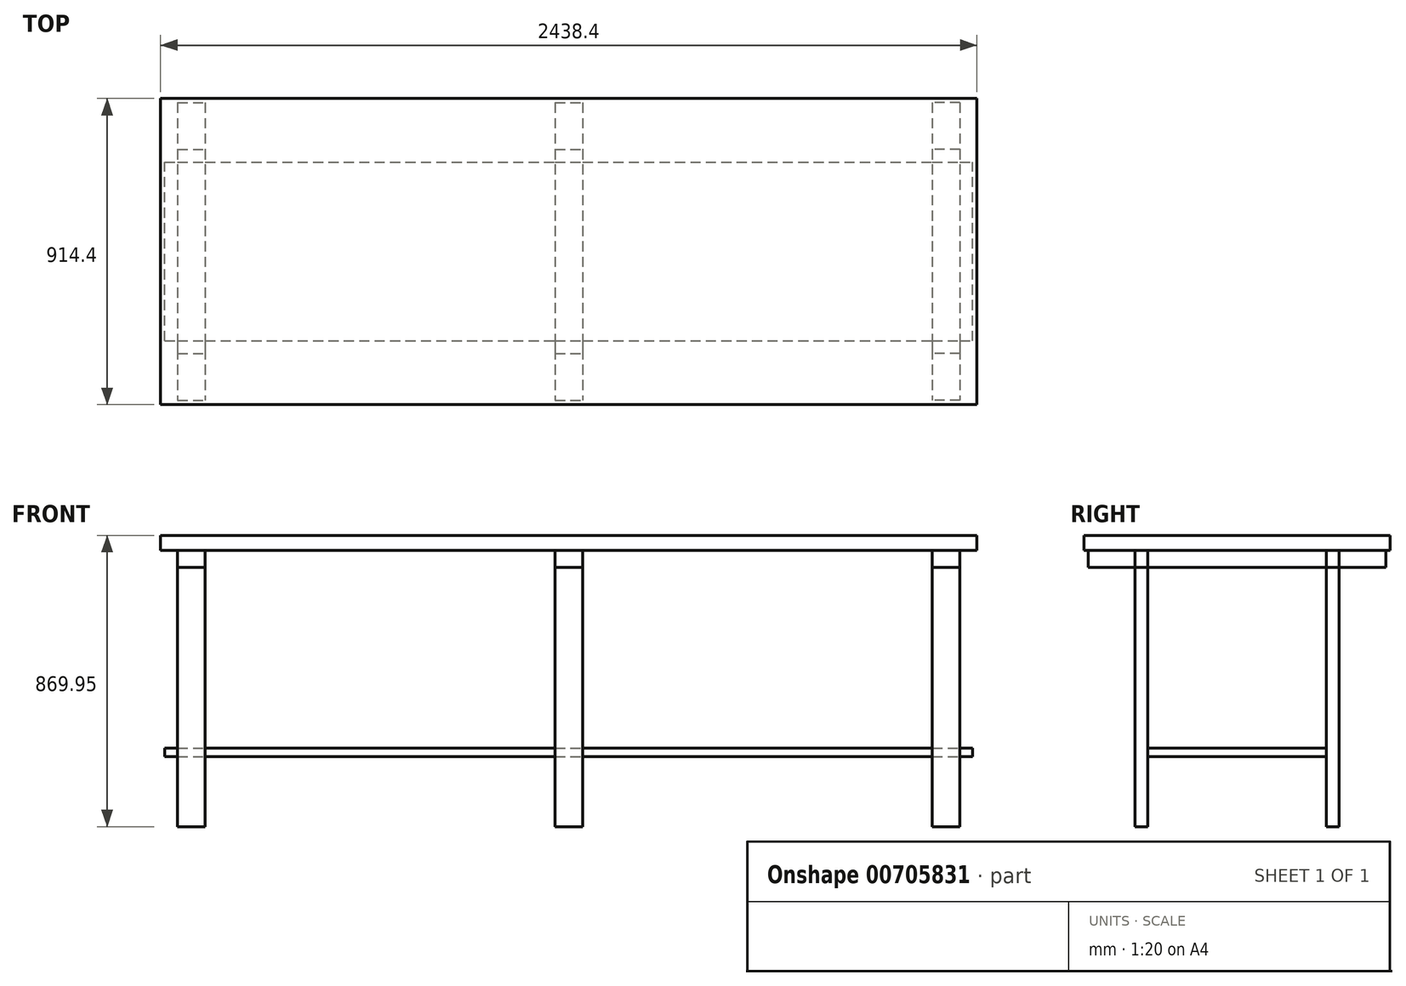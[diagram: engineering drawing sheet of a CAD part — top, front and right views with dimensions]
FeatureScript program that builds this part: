
annotation { "Feature Type Name" : "Feature", "Feature Type Description" : "" }
export const myFeature = defineFeature(function(context is Context, id is Id, definition is map)
    precondition{}
    {
        {
            var Q0;
            Q0=qCreatedBy(makeId("Top.planeOp"),FACE);
            var sketch = newSketch(context, id + "F0", { "sketchPlane" : qUnion([Q0])});
            skLineSegment(sketch, "E0.bottom", {"start": v(0, 0) * mm, "end": v(2438.4, 0) * mm});
            skLineSegment(sketch, "E0.top", {"start": v(0, 914.4) * mm, "end": v(2438.4, 914.4) * mm});
            skLineSegment(sketch, "E0.left", {"start": v(0, 0) * mm, "end": v(0, 914.4) * mm});
            skLineSegment(sketch, "E0.right", {"start": v(2438.4, 0) * mm, "end": v(2438.4, 914.4) * mm});
            skLineSegment(sketch, "E1.bottom", {"start": v(50.8, 901.7) * mm, "end": v(133.35, 901.7) * mm});
            skLineSegment(sketch, "E1.top", {"start": v(50.8, 12.7) * mm, "end": v(133.35, 12.7) * mm});
            skLineSegment(sketch, "E1.left", {"start": v(50.8, 901.7) * mm, "end": v(50.8, 12.7) * mm});
            skLineSegment(sketch, "E1.right", {"start": v(133.35, 901.7) * mm, "end": v(133.35, 12.7) * mm});
            skLineSegment(sketch, "E2", {"start": v(1219.2, 914.4) * mm, "end": v(1219.2, 0) * mm, "construction": true});
            skLineSegment(sketch, "E3", {"start": v(50.8, 762) * mm, "end": v(133.35, 762) * mm});
            skLineSegment(sketch, "E4", {"start": v(50.8, 723.9) * mm, "end": v(133.35, 723.9) * mm});
            skLineSegment(sketch, "E5", {"start": v(0, 457.2) * mm, "end": v(2438.4, 457.2) * mm, "construction": true});
            skLineSegment(sketch, "E6.MirrorCS", {"start": v(50.8, 152.4) * mm, "end": v(133.35, 152.4) * mm});
            skLineSegment(sketch, "E7.MirrorCS", {"start": v(50.8, 190.5) * mm, "end": v(133.35, 190.5) * mm});
            skLineSegment(sketch, "E8.MirrorCS", {"start": v(2387.6, 901.7) * mm, "end": v(2305.05, 901.7) * mm});
            skLineSegment(sketch, "E9.MirrorCS", {"start": v(2387.6, 12.7) * mm, "end": v(2305.05, 12.7) * mm});
            skLineSegment(sketch, "E10.MirrorCS", {"start": v(2387.6, 152.4) * mm, "end": v(2305.05, 152.4) * mm});
            skLineSegment(sketch, "E11.MirrorCS", {"start": v(2387.6, 190.5) * mm, "end": v(2305.05, 190.5) * mm});
            skLineSegment(sketch, "E12.MirrorCS", {"start": v(2387.6, 723.9) * mm, "end": v(2305.05, 723.9) * mm});
            skLineSegment(sketch, "E13.MirrorCS", {"start": v(2387.6, 762) * mm, "end": v(2305.05, 762) * mm});
            skLineSegment(sketch, "E14.MirrorCS", {"start": v(2387.6, 901.7) * mm, "end": v(2387.6, 12.7) * mm});
            skLineSegment(sketch, "E15.MirrorCS", {"start": v(2305.05, 901.7) * mm, "end": v(2305.05, 12.7) * mm});
            skLineSegment(sketch, "E16.bottom", {"start": v(1177.92, 901.7) * mm, "end": v(1260.48, 901.7) * mm});
            skLineSegment(sketch, "E16.top", {"start": v(1177.92, 12.7) * mm, "end": v(1260.48, 12.7) * mm});
            skLineSegment(sketch, "E16.left", {"start": v(1177.92, 901.7) * mm, "end": v(1177.92, 12.7) * mm});
            skLineSegment(sketch, "E16.right", {"start": v(1260.47, 901.7) * mm, "end": v(1260.47, 12.7) * mm});
            skLineSegment(sketch, "E17", {"start": v(1177.92, 762) * mm, "end": v(1260.48, 762) * mm});
            skLineSegment(sketch, "E18", {"start": v(1177.92, 723.9) * mm, "end": v(1260.48, 723.9) * mm});
            skLineSegment(sketch, "E19.MirrorCS", {"start": v(1177.92, 152.4) * mm, "end": v(1260.48, 152.4) * mm});
            skLineSegment(sketch, "E20.MirrorCS", {"start": v(1177.92, 190.5) * mm, "end": v(1260.48, 190.5) * mm});
            skPoint(sketch, "E21", {"position": v(1219.2, 901.7) * mm});
            skSolve(sketch);
        }
        {
            var Q0;
            Q0 = qSketchRegion(id + "F0", true);
            var Q1;
            {var subQ0=sQuery(id+"F0.wireOp",EDGE,"E1.bottom");Q1=makeQuery(id+"F0.imprint","IMPRINT",FACE,{"disambiguationData":[TD([[makeQuery(id+"F0.imprint","IMPRINT",EDGE,{"derivedFrom":subQ0}),-1.0]])]});}
            var Q2;
            {var subQ0=sQuery(id+"F0.wireOp",EDGE,"E3");Q2=makeQuery(id+"F0.imprint","IMPRINT",FACE,{"disambiguationData":[TD([[makeQuery(id+"F0.imprint","IMPRINT",EDGE,{"derivedFrom":subQ0}),-1.0]])]});}
            var Q3;
            {var subQ0=sQuery(id+"F0.wireOp",EDGE,"E4");Q3=makeQuery(id+"F0.imprint","IMPRINT",FACE,{"disambiguationData":[TD([[makeQuery(id+"F0.imprint","IMPRINT",EDGE,{"derivedFrom":subQ0}),-1.0]])]});}
            var Q4;
            {var subQ0=sQuery(id+"F0.wireOp",EDGE,"E6.MirrorCS");Q4=makeQuery(id+"F0.imprint","IMPRINT",FACE,{"disambiguationData":[TD([[makeQuery(id+"F0.imprint","IMPRINT",EDGE,{"derivedFrom":subQ0}),1.0]])]});}
            var Q5;
            {var subQ0=sQuery(id+"F0.wireOp",EDGE,"E1.top");Q5=makeQuery(id+"F0.imprint","IMPRINT",FACE,{"disambiguationData":[TD([[makeQuery(id+"F0.imprint","IMPRINT",EDGE,{"derivedFrom":subQ0}),1.0]])]});}
            var Q6;
            {var subQ0=sQuery(id+"F0.wireOp",EDGE,"E16.top");Q6=makeQuery(id+"F0.imprint","IMPRINT",FACE,{"disambiguationData":[TD([[makeQuery(id+"F0.imprint","IMPRINT",EDGE,{"derivedFrom":subQ0}),1.0]])]});}
            var Q7;
            {var subQ0=sQuery(id+"F0.wireOp",EDGE,"E19.MirrorCS");Q7=makeQuery(id+"F0.imprint","IMPRINT",FACE,{"disambiguationData":[TD([[makeQuery(id+"F0.imprint","IMPRINT",EDGE,{"derivedFrom":subQ0}),1.0]])]});}
            var Q8;
            {var subQ0=sQuery(id+"F0.wireOp",EDGE,"E18");Q8=makeQuery(id+"F0.imprint","IMPRINT",FACE,{"disambiguationData":[TD([[makeQuery(id+"F0.imprint","IMPRINT",EDGE,{"derivedFrom":subQ0}),-1.0]])]});}
            var Q9;
            {var subQ0=sQuery(id+"F0.wireOp",EDGE,"E17");Q9=makeQuery(id+"F0.imprint","IMPRINT",FACE,{"disambiguationData":[TD([[makeQuery(id+"F0.imprint","IMPRINT",EDGE,{"derivedFrom":subQ0}),-1.0]])]});}
            var Q10;
            {var subQ0=sQuery(id+"F0.wireOp",EDGE,"E16.bottom");Q10=makeQuery(id+"F0.imprint","IMPRINT",FACE,{"disambiguationData":[TD([[makeQuery(id+"F0.imprint","IMPRINT",EDGE,{"derivedFrom":subQ0}),-1.0]])]});}
            var Q11;
            {var subQ0=sQuery(id+"F0.wireOp",EDGE,"E8.MirrorCS");Q11=makeQuery(id+"F0.imprint","IMPRINT",FACE,{"disambiguationData":[TD([[makeQuery(id+"F0.imprint","IMPRINT",EDGE,{"derivedFrom":subQ0}),1.0]])]});}
            var Q12;
            {var subQ0=sQuery(id+"F0.wireOp",EDGE,"E12.MirrorCS");Q12=makeQuery(id+"F0.imprint","IMPRINT",FACE,{"disambiguationData":[TD([[makeQuery(id+"F0.imprint","IMPRINT",EDGE,{"derivedFrom":subQ0}),-1.0]])]});}
            var Q13;
            {var subQ0=sQuery(id+"F0.wireOp",EDGE,"E11.MirrorCS");Q13=makeQuery(id+"F0.imprint","IMPRINT",FACE,{"disambiguationData":[TD([[makeQuery(id+"F0.imprint","IMPRINT",EDGE,{"derivedFrom":subQ0}),-1.0]])]});}
            var Q14;
            {var subQ0=sQuery(id+"F0.wireOp",EDGE,"E10.MirrorCS");Q14=makeQuery(id+"F0.imprint","IMPRINT",FACE,{"disambiguationData":[TD([[makeQuery(id+"F0.imprint","IMPRINT",EDGE,{"derivedFrom":subQ0}),-1.0]])]});}
            var Q15;
            {var subQ0=sQuery(id+"F0.wireOp",EDGE,"E9.MirrorCS");Q15=makeQuery(id+"F0.imprint","IMPRINT",FACE,{"disambiguationData":[TD([[makeQuery(id+"F0.imprint","IMPRINT",EDGE,{"derivedFrom":subQ0}),-1.0]])]});}
            extrude(context, id + "F1", {"entities" : qUnion([Q0, Q1, Q2, Q3, Q4, Q5, Q6, Q7, Q8, Q9, Q10, Q11, Q12, Q13, Q14, Q15]), "depth" : 44.45 * mm, "offsetDistance" : 25.4 * mm});
        }
        {
            var Q0;
            {var subQ0=sQuery(id+"F0.wireOp",EDGE,"E1.top");Q0=makeQuery(id+"F0.imprint","IMPRINT",FACE,{"disambiguationData":[TD([[makeQuery(id+"F0.imprint","IMPRINT",EDGE,{"derivedFrom":subQ0}),1.0]])]});}
            var Q1;
            {var subQ0=sQuery(id+"F0.wireOp",EDGE,"E6.MirrorCS");Q1=makeQuery(id+"F0.imprint","IMPRINT",FACE,{"disambiguationData":[TD([[makeQuery(id+"F0.imprint","IMPRINT",EDGE,{"derivedFrom":subQ0}),1.0]])]});}
            var Q2;
            {var subQ0=sQuery(id+"F0.wireOp",EDGE,"E4");Q2=makeQuery(id+"F0.imprint","IMPRINT",FACE,{"disambiguationData":[TD([[makeQuery(id+"F0.imprint","IMPRINT",EDGE,{"derivedFrom":subQ0}),-1.0]])]});}
            var Q3;
            {var subQ0=sQuery(id+"F0.wireOp",EDGE,"E3");Q3=makeQuery(id+"F0.imprint","IMPRINT",FACE,{"disambiguationData":[TD([[makeQuery(id+"F0.imprint","IMPRINT",EDGE,{"derivedFrom":subQ0}),-1.0]])]});}
            var Q4;
            {var subQ0=sQuery(id+"F0.wireOp",EDGE,"E1.bottom");Q4=makeQuery(id+"F0.imprint","IMPRINT",FACE,{"disambiguationData":[TD([[makeQuery(id+"F0.imprint","IMPRINT",EDGE,{"derivedFrom":subQ0}),-1.0]])]});}
            var Q5;
            {var subQ0=sQuery(id+"F0.wireOp",EDGE,"E16.top");Q5=makeQuery(id+"F0.imprint","IMPRINT",FACE,{"disambiguationData":[TD([[makeQuery(id+"F0.imprint","IMPRINT",EDGE,{"derivedFrom":subQ0}),1.0]])]});}
            var Q6;
            {var subQ0=sQuery(id+"F0.wireOp",EDGE,"E18");Q6=makeQuery(id+"F0.imprint","IMPRINT",FACE,{"disambiguationData":[TD([[makeQuery(id+"F0.imprint","IMPRINT",EDGE,{"derivedFrom":subQ0}),-1.0]])]});}
            var Q7;
            {var subQ0=sQuery(id+"F0.wireOp",EDGE,"E19.MirrorCS");Q7=makeQuery(id+"F0.imprint","IMPRINT",FACE,{"disambiguationData":[TD([[makeQuery(id+"F0.imprint","IMPRINT",EDGE,{"derivedFrom":subQ0}),1.0]])]});}
            var Q8;
            {var subQ0=sQuery(id+"F0.wireOp",EDGE,"E17");Q8=makeQuery(id+"F0.imprint","IMPRINT",FACE,{"disambiguationData":[TD([[makeQuery(id+"F0.imprint","IMPRINT",EDGE,{"derivedFrom":subQ0}),-1.0]])]});}
            var Q9;
            {var subQ0=sQuery(id+"F0.wireOp",EDGE,"E16.bottom");Q9=makeQuery(id+"F0.imprint","IMPRINT",FACE,{"disambiguationData":[TD([[makeQuery(id+"F0.imprint","IMPRINT",EDGE,{"derivedFrom":subQ0}),-1.0]])]});}
            var Q10;
            {var subQ0=sQuery(id+"F0.wireOp",EDGE,"E9.MirrorCS");Q10=makeQuery(id+"F0.imprint","IMPRINT",FACE,{"disambiguationData":[TD([[makeQuery(id+"F0.imprint","IMPRINT",EDGE,{"derivedFrom":subQ0}),-1.0]])]});}
            var Q11;
            {var subQ0=sQuery(id+"F0.wireOp",EDGE,"E10.MirrorCS");Q11=makeQuery(id+"F0.imprint","IMPRINT",FACE,{"disambiguationData":[TD([[makeQuery(id+"F0.imprint","IMPRINT",EDGE,{"derivedFrom":subQ0}),-1.0]])]});}
            var Q12;
            {var subQ0=sQuery(id+"F0.wireOp",EDGE,"E11.MirrorCS");Q12=makeQuery(id+"F0.imprint","IMPRINT",FACE,{"disambiguationData":[TD([[makeQuery(id+"F0.imprint","IMPRINT",EDGE,{"derivedFrom":subQ0}),-1.0]])]});}
            var Q13;
            {var subQ0=sQuery(id+"F0.wireOp",EDGE,"E12.MirrorCS");Q13=makeQuery(id+"F0.imprint","IMPRINT",FACE,{"disambiguationData":[TD([[makeQuery(id+"F0.imprint","IMPRINT",EDGE,{"derivedFrom":subQ0}),-1.0]])]});}
            var Q14;
            {var subQ0=sQuery(id+"F0.wireOp",EDGE,"E8.MirrorCS");Q14=makeQuery(id+"F0.imprint","IMPRINT",FACE,{"disambiguationData":[TD([[makeQuery(id+"F0.imprint","IMPRINT",EDGE,{"derivedFrom":subQ0}),1.0]])]});}
            extrude(context, id + "F2", {"entities" : qUnion([Q0, Q1, Q2, Q3, Q4, Q5, Q6, Q7, Q8, Q9, Q10, Q11, Q12, Q13, Q14]), "operationType" : NewBodyOperationType.ADD, "oppositeDirection" : true, "depth" : 50.8 * mm, "offsetDistance" : 25.4 * mm});
        }
        {
            var Q0;
            {var subQ0=sQuery(id+"F0.wireOp",EDGE,"E6.MirrorCS");Q0=makeQuery(id+"F0.imprint","IMPRINT",FACE,{"disambiguationData":[TD([[makeQuery(id+"F0.imprint","IMPRINT",EDGE,{"derivedFrom":subQ0}),1.0]])]});}
            var Q1;
            {var subQ0=sQuery(id+"F0.wireOp",EDGE,"E3");Q1=makeQuery(id+"F0.imprint","IMPRINT",FACE,{"disambiguationData":[TD([[makeQuery(id+"F0.imprint","IMPRINT",EDGE,{"derivedFrom":subQ0}),-1.0]])]});}
            var Q2;
            {var subQ0=sQuery(id+"F0.wireOp",EDGE,"E19.MirrorCS");Q2=makeQuery(id+"F0.imprint","IMPRINT",FACE,{"disambiguationData":[TD([[makeQuery(id+"F0.imprint","IMPRINT",EDGE,{"derivedFrom":subQ0}),1.0]])]});}
            var Q3;
            {var subQ0=sQuery(id+"F0.wireOp",EDGE,"E17");Q3=makeQuery(id+"F0.imprint","IMPRINT",FACE,{"disambiguationData":[TD([[makeQuery(id+"F0.imprint","IMPRINT",EDGE,{"derivedFrom":subQ0}),-1.0]])]});}
            var Q4;
            {var subQ0=sQuery(id+"F0.wireOp",EDGE,"E10.MirrorCS");Q4=makeQuery(id+"F0.imprint","IMPRINT",FACE,{"disambiguationData":[TD([[makeQuery(id+"F0.imprint","IMPRINT",EDGE,{"derivedFrom":subQ0}),-1.0]])]});}
            var Q5;
            {var subQ0=sQuery(id+"F0.wireOp",EDGE,"E12.MirrorCS");Q5=makeQuery(id+"F0.imprint","IMPRINT",FACE,{"disambiguationData":[TD([[makeQuery(id+"F0.imprint","IMPRINT",EDGE,{"derivedFrom":subQ0}),-1.0]])]});}
            extrude(context, id + "F3", {"entities" : qUnion([Q0, Q1, Q2, Q3, Q4, Q5]), "oppositeDirection" : true, "depth" : 825.5 * mm, "offsetDistance" : 25.4 * mm});
        }
        {
            var Q0;
            Q0=makeQuery(id+"F0.imprint","IMPRINT",FACE,{"disambiguationData":[TD([[makeQuery(id+"F0.imprint","IMPRINT",EDGE,{"derivedFrom":sQuery(id+"F0.wireOp",EDGE,"E0.bottom")}),1.0]])]});
            cPlane(context, id + "F4", {"entities" : qUnion([Q0]), "cplaneType" : CPlaneType.OFFSET, "offset" : 590.55 * mm, "oppositeDirection" : true, "width" : 152.4 * mm, "height" : 152.4 * mm});
        }
        {
            var Q0;
            Q0=qCreatedBy(id+"F4.planeOp",FACE);
            var sketch = newSketch(context, id + "F5", { "sketchPlane" : qUnion([Q0])});
            skLineSegment(sketch, "E22.0.0", {"start": v(50.8, 723.9) * mm, "end": v(50.8, 190.5) * mm});
            skLineSegment(sketch, "E22.0.1", {"start": v(50.8, 190.5) * mm, "end": v(133.35, 190.5) * mm});
            skLineSegment(sketch, "E22.0.2", {"start": v(133.35, 190.5) * mm, "end": v(133.35, 723.9) * mm});
            skLineSegment(sketch, "E22.0.3", {"start": v(133.35, 723.9) * mm, "end": v(50.8, 723.9) * mm});
            skLineSegment(sketch, "E23.0.0", {"start": v(2305.05, 190.5) * mm, "end": v(2387.6, 190.5) * mm});
            skLineSegment(sketch, "E23.0.1", {"start": v(2387.6, 190.5) * mm, "end": v(2387.6, 723.9) * mm});
            skLineSegment(sketch, "E23.0.2", {"start": v(2387.6, 723.9) * mm, "end": v(2305.05, 723.9) * mm});
            skLineSegment(sketch, "E23.0.3", {"start": v(2305.05, 723.9) * mm, "end": v(2305.05, 190.5) * mm});
            skLineSegment(sketch, "E24.bottom", {"start": v(12.7, 190.5) * mm, "end": v(2425.7, 190.5) * mm});
            skLineSegment(sketch, "E24.top", {"start": v(12.7, 723.9) * mm, "end": v(2425.7, 723.9) * mm});
            skLineSegment(sketch, "E24.left", {"start": v(12.7, 190.5) * mm, "end": v(12.7, 723.9) * mm});
            skLineSegment(sketch, "E24.right", {"start": v(2425.7, 190.5) * mm, "end": v(2425.7, 723.9) * mm});
            skSolve(sketch);
        }
        {
            var Q0;
            {var subQ0=sQuery(id+"F5.wireOp",EDGE,"E22.0.2");Q0=makeQuery(id+"F5.imprint","IMPRINT",FACE,{"disambiguationData":[TD([[makeQuery(id+"F5.imprint","IMPRINT",EDGE,{"derivedFrom":subQ0}),-1.0]])]});}
            var Q1;
            {var subQ0=sQuery(id+"F5.wireOp",EDGE,"E22.0.0");Q1=makeQuery(id+"F5.imprint","IMPRINT",FACE,{"disambiguationData":[TD([[makeQuery(id+"F5.imprint","IMPRINT",EDGE,{"derivedFrom":subQ0}),1.0]])]});}
            var Q2;
            {var subQ0=sQuery(id+"F5.wireOp",EDGE,"E22.0.0");Q2=makeQuery(id+"F5.imprint","IMPRINT",FACE,{"disambiguationData":[TD([[makeQuery(id+"F5.imprint","IMPRINT",EDGE,{"derivedFrom":subQ0}),-1.0]])]});}
            var Q3;
            {var subQ0=sQuery(id+"F5.wireOp",EDGE,"E23.0.1");Q3=makeQuery(id+"F5.imprint","IMPRINT",FACE,{"disambiguationData":[TD([[makeQuery(id+"F5.imprint","IMPRINT",EDGE,{"derivedFrom":subQ0}),1.0]])]});}
            var Q4;
            {var subQ0=sQuery(id+"F5.wireOp",EDGE,"E23.0.1");Q4=makeQuery(id+"F5.imprint","IMPRINT",FACE,{"disambiguationData":[TD([[makeQuery(id+"F5.imprint","IMPRINT",EDGE,{"derivedFrom":subQ0}),-1.0]])]});}
            extrude(context, id + "F6", {"entities" : qUnion([Q0, Q1, Q2, Q3, Q4]), "operationType" : NewBodyOperationType.ADD, "oppositeDirection" : true, "depth" : 25.4 * mm, "offsetDistance" : 25.4 * mm});
        }
    });
